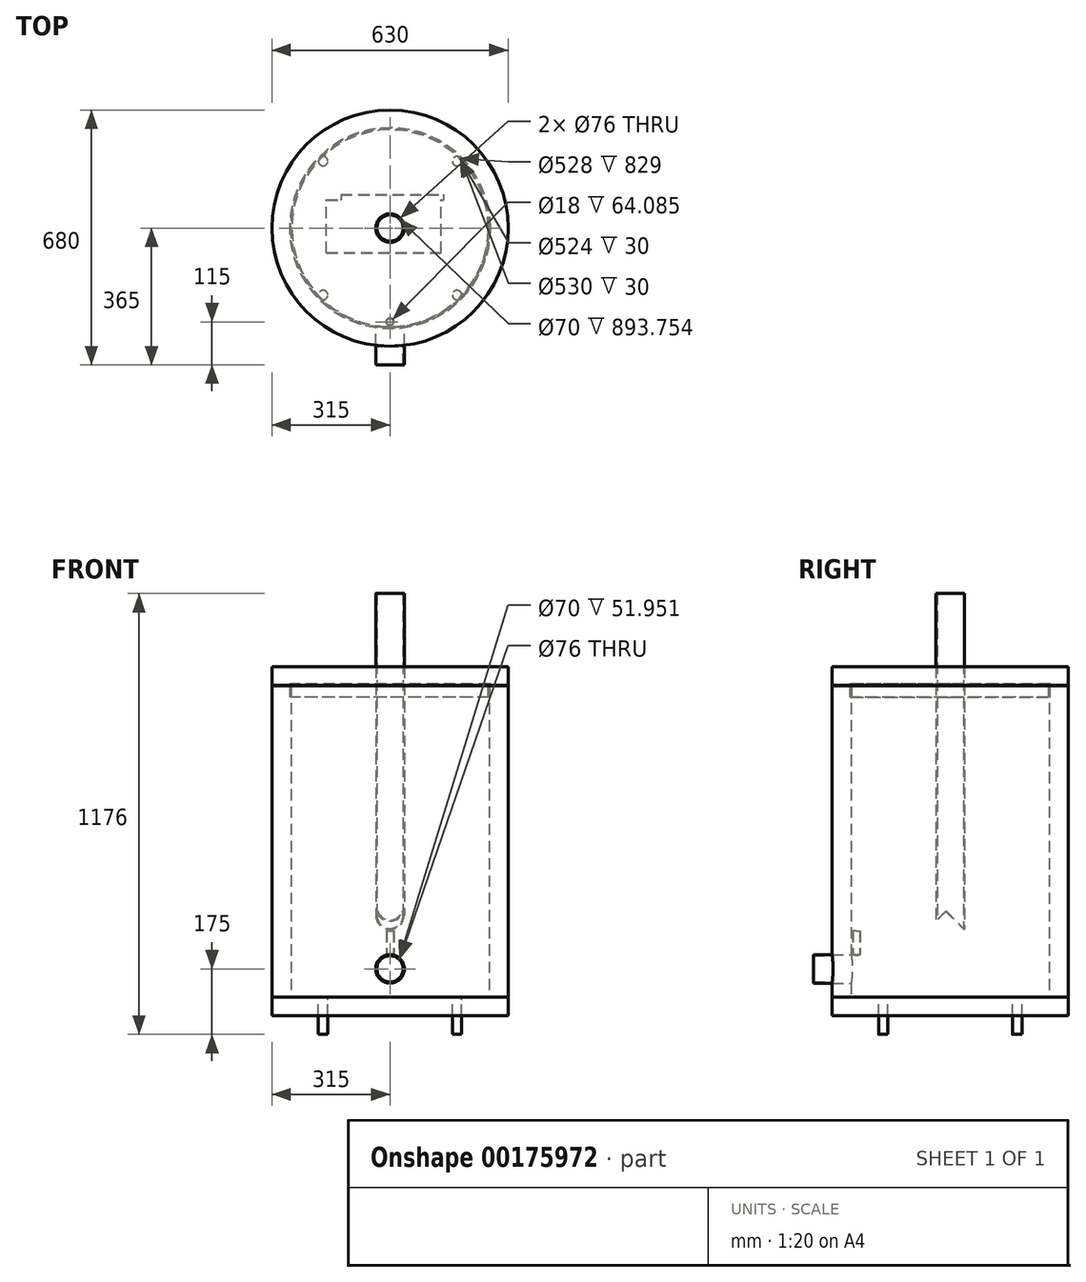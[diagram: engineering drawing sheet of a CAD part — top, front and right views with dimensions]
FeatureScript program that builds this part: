
annotation { "Feature Type Name" : "Feature", "Feature Type Description" : "" }
export const myFeature = defineFeature(function(context is Context, id is Id, definition is map)
    precondition{}
    {
        {
            assignVariable(context, id + "F0", {"name" : "Diameter", "anyValue" : 530});
        }
        {
            assignVariable(context, id + "F1", {"name" : "Length", "anyValue" : 415 * 2});
        }
        {
            assignVariable(context, id + "F2", {"name" : "TubeOD", "anyValue" : 76});
        }
        {
            var Q0;
            Q0=qCreatedBy(makeId("Top.planeOp"),FACE);
            var sketch = newSketch(context, id + "F3", { "sketchPlane" : qUnion([Q0])});
            skCircle(sketch, "E0", {"center": v(0, 0) * mm, "radius": 265 * mm});
            skSolve(sketch);
        }
        {
            var Q0;
            Q0 = qSketchRegion(id + "F3", true);
            extrude(context, id + "F4", {"entities" : qUnion([Q0]), "depth" : (getVariable(context, 'Length') - 15) * mm});
        }
        {
            var Q0;
            Q0=makeQuery(id+"F4.opExtrude","CAP_FACE",FACE,{"disambiguationData":[OSD([sQuery(id+"F3.wireOp",EDGE,"E0")])],"isStart":false});
            shell(context, id + "F5", {"entities" : qUnion([Q0]), "thickness" : 1 * mm});
        }
        {
            var Q0;
            Q0=qCreatedBy(makeId("Front.planeOp"),FACE);
            var sketch = newSketch(context, id + "F6", { "sketchPlane" : qUnion([Q0])});
            skCircle(sketch, "E1", {"center": v(0, 75) * mm, "radius": 38 * mm});
            skCircle(sketch, "E2", {"center": v(0, 75) * mm, "radius": 35 * mm});
            skSolve(sketch);
        }
        {
            var Q0;
            Q0 = qSketchRegion(id + "F6", true);
            extrude(context, id + "F7", {"entities" : qUnion([Q0]), "depth" : (getVariable(context, 'Diameter') / 2 + 100) * mm, "hasSecondDirection" : true, "secondDirectionOppositeDirection" : true, "secondDirectionDepth" : (getVariable(context, 'TubeOD') / 2) * mm});
        }
        {
            var Q0;
            {var subQ0=sQuery(id+"F3.wireOp",EDGE,"E0");Q0=makeQuery(id+"F5.opShell","OFFSET_FACE",FACE,{"disambiguationData":[OSD([subQ0]),TDD([makeQuery(id+"F4.opExtrude","CAP_FACE",FACE,{"disambiguationData":[OSD([subQ0])],"isStart":true})])]});}
            cPlane(context, id + "F8", {"entities" : qUnion([Q0]), "cplaneType" : CPlaneType.OFFSET, "offset" : 75 * mm, "width" : 150 * mm, "height" : 150 * mm});
        }
        {
            var Q0;
            Q0=qCreatedBy(id+"F8.planeOp",FACE);
            var sketch = newSketch(context, id + "F9", { "sketchPlane" : qUnion([Q0])});
            skCircle(sketch, "E3", {"center": v(0, 0) * mm, "radius": 38 * mm});
            skCircle(sketch, "E4", {"center": v(0, 0) * mm, "radius": 35 * mm});
            skSolve(sketch);
        }
        {
            var Q0;
            Q0 = qSketchRegion(id + "F9", true);
            extrude(context, id + "F10", {"entities" : qUnion([Q0]), "depth" : 1000 * mm, "hasSecondDirection" : true, "secondDirectionOppositeDirection" : true, "secondDirectionDepth" : (getVariable(context, 'TubeOD') / 2) * mm});
        }
        {
            var Q0;
            Q0=qCreatedBy(makeId("Top.planeOp"),FACE);
            var sketch = newSketch(context, id + "F11", { "sketchPlane" : qUnion([Q0])});
            skCircle(sketch, "E5", {"center": v(0, 0) * mm, "radius": 315 * mm});
            skCircle(sketch, "E6", {"center": v(0, 0) * mm, "radius": 265 * mm});
            skSolve(sketch);
        }
        {
            var Q0;
            Q0 = qSketchRegion(id + "F11", true);
            extrude(context, id + "F12", {"entities" : qUnion([Q0]), "depth" : (getVariable(context, 'Length')) * mm});
        }
        {
            var Q0;
            Q0=qCreatedBy(id+"F8.planeOp",FACE);
            var sketch = newSketch(context, id + "F13", { "sketchPlane" : qUnion([Q0])});
            skLineSegment(sketch, "E7", {"start": v(0, 0) * mm, "end": v(0, -500) * mm, "construction": true});
            skCircle(sketch, "E8", {"center": v(0, -250) * mm, "radius": 10 * mm});
            skCircle(sketch, "E9", {"center": v(0, -250) * mm, "radius": 9 * mm});
            skSolve(sketch);
        }
        {
            var Q0;
            Q0 = qSketchRegion(id + "F13", true);
            extrude(context, id + "F14", {"entities" : qUnion([Q0]), "depth" : 100 * mm});
        }
        {
            var Q0;
            Q0=makeQuery(id+"F10.opExtrude","CAP_FACE",FACE,{"disambiguationData":[OSD([sQuery(id+"F9.wireOp",EDGE,"E3"),sQuery(id+"F9.wireOp",EDGE,"E4")])],"isStart":true});
            var Q1;
            Q1=makeQuery(id+"F7.opExtrude","CAP_FACE",FACE,{"disambiguationData":[OSD([sQuery(id+"F6.wireOp",EDGE,"E1"),sQuery(id+"F6.wireOp",EDGE,"E2")])],"isStart":true});
            cPlane(context, id + "F15", {"entities" : qUnion([Q0, Q1]), "cplaneType" : CPlaneType.MID_PLANE, "offset" : 25 * mm, "width" : 150 * mm, "height" : 150 * mm});
        }
        {
            var Q0;
            Q0=qCreatedBy(id+"F15.planeOp",FACE);
            var sketch = newSketch(context, id + "F16", { "sketchPlane" : qUnion([Q0])});
            skLineSegment(sketch, "E10.bottom", {"start": v(142.94, 169.92) * mm, "end": v(-130.86, 169.92) * mm});
            skLineSegment(sketch, "E10.top", {"start": v(142.94, -62.97) * mm, "end": v(-130.86, -62.97) * mm});
            skLineSegment(sketch, "E10.left", {"start": v(142.94, 169.92) * mm, "end": v(142.94, -62.97) * mm});
            skLineSegment(sketch, "E10.right", {"start": v(-130.86, 169.92) * mm, "end": v(-130.86, -62.97) * mm});
            skSolve(sketch);
        }
        {
            var Q0;
            Q0 = qSketchRegion(id + "F16", true);
            extrude(context, id + "F17", {"entities" : qUnion([Q0]), "operationType" : NewBodyOperationType.REMOVE, "oppositeDirection" : true, "depth" : 100 * mm});
        }
        {
            var Q0;
            Q0=qCreatedBy(id+"F15.planeOp",FACE);
            var sketch = newSketch(context, id + "F18", { "sketchPlane" : qUnion([Q0])});
            skLineSegment(sketch, "E11.bottom", {"start": v(136.43, 190.22) * mm, "end": v(-169.38, 190.22) * mm});
            skLineSegment(sketch, "E11.top", {"start": v(136.43, -87.4) * mm, "end": v(-169.38, -87.4) * mm});
            skLineSegment(sketch, "E11.left", {"start": v(136.43, 190.22) * mm, "end": v(136.43, -87.4) * mm});
            skLineSegment(sketch, "E11.right", {"start": v(-169.38, 190.22) * mm, "end": v(-169.38, -87.4) * mm});
            skSolve(sketch);
        }
        {
            var Q0;
            Q0 = qSketchRegion(id + "F18", true);
            extrude(context, id + "F19", {"entities" : qUnion([Q0]), "operationType" : NewBodyOperationType.REMOVE, "depth" : 100 * mm});
        }
        {
            var Q0;
            Q0=qCreatedBy(makeId("Front.planeOp"),FACE);
            var sketch = newSketch(context, id + "F20", { "sketchPlane" : qUnion([Q0])});
            skCircle(sketch, "E12.0", {"center": v(0, 75) * mm, "radius": 38 * mm});
            skSolve(sketch);
        }
        {
            var Q0;
            Q0 = qSketchRegion(id + "F20", true);
            var Q1;
            Q1=makeQuery(id+"F4.opExtrude","SWEPT_FACE",FACE,{"disambiguationData":[OSD([sQuery(id+"F3.wireOp",EDGE,"E0")])]});
            extrude(context, id + "F21", {"entities" : qUnion([Q0]), "operationType" : NewBodyOperationType.REMOVE, "endBound" : BoundingType.UP_TO_SURFACE, "endBoundEntityFace" : qUnion([Q1]), "depth" : 25 * mm});
        }
        {
            var Q0;
            Q0=qCreatedBy(makeId("Right.planeOp"),FACE);
            var sketch = newSketch(context, id + "F22", { "sketchPlane" : qUnion([Q0])});
            skLineSegment(sketch, "E13", {"start": v(265, 815) * mm, "end": v(265, 0) * mm, "construction": true});
            skLineSegment(sketch, "E14", {"start": v(38, 1076) * mm, "end": v(38, 38) * mm, "construction": true});
            skLineSegment(sketch, "E15", {"start": v(38, 830) * mm, "end": v(268, 830) * mm});
            skArc(sketch, "E16", {"start": v(268, 833.48) * mm, "mid": v(266, 835.46) * mm, "end": v(264, 833.48) * mm});
            skLineSegment(sketch, "E17", {"start": v(261.5, 831) * mm, "end": v(38, 831) * mm});
            skLineSegment(sketch, "E18", {"start": v(38, 831) * mm, "end": v(38, 830) * mm});
            skArc(sketch, "E19", {"start": v(261.5, 831) * mm, "mid": v(263.26, 831.73) * mm, "end": v(264, 833.48) * mm});
            skLineSegment(sketch, "E20", {"start": v(268, 833.48) * mm, "end": v(268, 830) * mm});
            skSolve(sketch);
        }
        {
            var Q0;
            Q0 = qSketchRegion(id + "F22", true);
            var Q1;
            Q1=makeQuery(id+"F10.opExtrude","SWEPT_FACE",FACE,{"disambiguationData":[OSD([sQuery(id+"F9.wireOp",EDGE,"E3")])]});
            revolve(context, id + "F23", {"entities" : qUnion([Q0]), "axis" : qUnion([Q1]), "revolveType" : RevolveType.FULL});
        }
        {
            var Q0;
            Q0=qCreatedBy(makeId("Right.planeOp"),FACE);
            var sketch = newSketch(context, id + "F24", { "sketchPlane" : qUnion([Q0])});
            skLineSegment(sketch, "E21.bottom", {"start": v(265, 830) * mm, "end": v(264, 830) * mm});
            skLineSegment(sketch, "E21.top", {"start": v(265, 815) * mm, "end": v(264, 815) * mm});
            skLineSegment(sketch, "E21.left", {"start": v(265, 830) * mm, "end": v(265, 815) * mm});
            skLineSegment(sketch, "E21.right", {"start": v(264, 830) * mm, "end": v(264, 815) * mm});
            skSolve(sketch);
        }
        {
            var Q0;
            Q0 = qSketchRegion(id + "F24", true);
            var Q1;
            Q1=makeQuery(id+"F10.opExtrude","SWEPT_FACE",FACE,{"disambiguationData":[OSD([sQuery(id+"F9.wireOp",EDGE,"E3")])]});
            revolve(context, id + "F25", {"operationType" : NewBodyOperationType.ADD, "entities" : qUnion([Q0]), "axis" : qUnion([Q1]), "revolveType" : RevolveType.FULL});
        }
        {
            var Q0;
            Q0=qCreatedBy(makeId("Right.planeOp"),FACE);
            var sketch = newSketch(context, id + "F26", { "sketchPlane" : qUnion([Q0])});
            skLineSegment(sketch, "E22.bottom", {"start": v(267, 830) * mm, "end": v(265, 830) * mm});
            skLineSegment(sketch, "E22.top", {"start": v(267, 800) * mm, "end": v(265, 800) * mm});
            skLineSegment(sketch, "E22.left", {"start": v(267, 830) * mm, "end": v(267, 800) * mm});
            skLineSegment(sketch, "E22.right", {"start": v(265, 830) * mm, "end": v(265, 800) * mm});
            skSolve(sketch);
        }
        {
            var Q0;
            Q0 = qSketchRegion(id + "F26", true);
            var Q1;
            Q1=makeQuery(id+"F10.opExtrude","SWEPT_FACE",FACE,{"disambiguationData":[OSD([sQuery(id+"F9.wireOp",EDGE,"E3")])]});
            revolve(context, id + "F27", {"entities" : qUnion([Q0]), "axis" : qUnion([Q1]), "revolveType" : RevolveType.FULL});
        }
        {
            var Q0;
            Q0=qCreatedBy(makeId("Right.planeOp"),FACE);
            var sketch = newSketch(context, id + "F28", { "sketchPlane" : qUnion([Q0])});
            skLineSegment(sketch, "E23.bottom", {"start": v(264, 830) * mm, "end": v(262, 830) * mm});
            skLineSegment(sketch, "E23.top", {"start": v(264, 800) * mm, "end": v(262, 800) * mm});
            skLineSegment(sketch, "E23.left", {"start": v(264, 830) * mm, "end": v(264, 800) * mm});
            skLineSegment(sketch, "E23.right", {"start": v(262, 830) * mm, "end": v(262, 800) * mm});
            skSolve(sketch);
        }
        {
            var Q0;
            Q0 = qSketchRegion(id + "F28", true);
            var Q1;
            Q1=makeQuery(id+"F10.opExtrude","SWEPT_FACE",FACE,{"disambiguationData":[OSD([sQuery(id+"F9.wireOp",EDGE,"E3")])]});
            revolve(context, id + "F29", {"entities" : qUnion([Q0]), "axis" : qUnion([Q1]), "revolveType" : RevolveType.FULL});
        }
        {
            var Q0;
            Q0=makeQuery(id+"F4.opExtrude","CAP_FACE",FACE,{"disambiguationData":[OSD([sQuery(id+"F3.wireOp",EDGE,"E0")])],"isStart":true});
            var sketch = newSketch(context, id + "F30", { "sketchPlane" : qUnion([Q0])});
            skCircle(sketch, "E24", {"center": v(-178.54, 178.54) * mm, "radius": 12.5 * mm});
            skLineSegment(sketch, "E25", {"start": v(0, 0) * mm, "end": v(0, 259.15) * mm, "construction": true});
            skLineSegment(sketch, "E26", {"start": v(0, 0) * mm, "end": v(-178.54, 178.54) * mm, "construction": true});
            skCircle(sketch, "E27.1.0", {"center": v(-178.54, -178.54) * mm, "radius": 12.5 * mm});
            skCircle(sketch, "E27.2.0", {"center": v(178.54, -178.54) * mm, "radius": 12.5 * mm});
            skCircle(sketch, "E27.3.0", {"center": v(178.54, 178.54) * mm, "radius": 12.5 * mm});
            skPoint(sketch, "E27.center", {"position": v(0, 0) * mm});
            skSolve(sketch);
        }
        {
            var Q0;
            Q0 = qSketchRegion(id + "F30", true);
            extrude(context, id + "F31", {"entities" : qUnion([Q0]), "operationType" : NewBodyOperationType.ADD, "depth" : 100 * mm});
        }
        {
            var Q0;
            Q0=makeQuery(id+"F4.opExtrude","CAP_FACE",FACE,{"disambiguationData":[OSD([sQuery(id+"F3.wireOp",EDGE,"E0")])],"isStart":true});
            var sketch = newSketch(context, id + "F32", { "sketchPlane" : qUnion([Q0])});
            skCircle(sketch, "E28", {"center": v(0, 0) * mm, "radius": 315 * mm});
            skSolve(sketch);
        }
        {
            var Q0;
            Q0 = qSketchRegion(id + "F32", true);
            extrude(context, id + "F33", {"entities" : qUnion([Q0]), "depth" : 50 * mm});
        }
        {
            var Q0;
            Q0=makeQuery(id+"F23.opRevolve","SWEPT_FACE",FACE,{"disambiguationData":[OSD([sQuery(id+"F22.wireOp",EDGE,"E17")])]});
            var sketch = newSketch(context, id + "F34", { "sketchPlane" : qUnion([Q0])});
            skCircle(sketch, "E29", {"center": v(0, 0) * mm, "radius": 315 * mm});
            skCircle(sketch, "E30", {"center": v(0, 0) * mm, "radius": 38 * mm});
            skSolve(sketch);
        }
        {
            var Q0;
            Q0 = qSketchRegion(id + "F34", true);
            extrude(context, id + "F35", {"entities" : qUnion([Q0]), "depth" : 50 * mm});
        }
        {
            var Q0;
            Q0=qCreatedBy(makeId("Front.planeOp"),FACE);
            var sketch = newSketch(context, id + "F36", { "sketchPlane" : qUnion([Q0])});
            skCircle(sketch, "E31.0", {"center": v(0, 75) * mm, "radius": 38 * mm});
            skSolve(sketch);
        }
        {
            var Q0;
            Q0 = qSketchRegion(id + "F36", true);
            var Q1;
            Q1=makeQuery(id+"F12.opExtrude","SWEPT_FACE",FACE,{"disambiguationData":[OSD([sQuery(id+"F11.wireOp",EDGE,"E5")])]});
            extrude(context, id + "F37", {"entities" : qUnion([Q0]), "operationType" : NewBodyOperationType.REMOVE, "endBound" : BoundingType.UP_TO_SURFACE, "endBoundEntityFace" : qUnion([Q1]), "depth" : 25 * mm});
        }
    });
